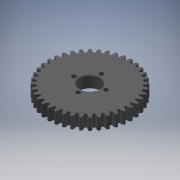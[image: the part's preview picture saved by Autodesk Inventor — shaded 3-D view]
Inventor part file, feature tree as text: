
AUTODESK INVENTOR PART (.ipt)
format: ipt  version: 2016 (Build 200138000, 138)  size: 1,243,136 bytes
history: native  units: mm
features: other x14, sketch x4, revolve x3, extrude x2, hole x1
ambient origin geometry x8: Origin, YZ Plane, XZ Plane, XY Plane, X Axis, Y Axis, Z Axis, Center Point
bodies: Solid1 (feature_tree)
feature tree (24):
  revolve  "Revolution1"  [1 undecoded]
  extrude  "Extrusion1"  TaperAngle=360.0deg  [1 undecoded]
  hole  "Hole1"  [1 undecoded]
  revolve  "Revolution2"  [1 undecoded]
  revolve  "Revolution3"  [1 undecoded]
  other  "b_XY"
  other  "b_YZ"
  other  "b_ZX"
  other  "b_X"
  other  "b_Y"
  other  "b_Z"
  other  "b_Center"
  other  "turn_around_XY"
  other  "turn_around_YZ"
  other  "turn_around_ZX"
  other  "turn_around_X"
  other  "turn_around_Y"
  other  "turn_around_Z"
  other  "turn_around_Center"
  extrude  "押し出し2"  Depth=6.0mm
  sketch  "Sketch_12"  dims[d11=360.0deg d12=0.0mm d13=14.0mm d14=2.2mm d15=2.2mm d16=2.2mm d17=2.2mm d18=6.0mm d19=0.0mm]
  sketch  "Sketch_3"  dims[d0=360.0deg d1=6.0mm d2=0.0mm]
  sketch  "Sketch3"  dims[d3=10.0mm d4=6.0mm d5=4.0mm d6=2.0mm d7=90.0deg d8=6.0mm d9=0.0mm d10=360.0deg]
  sketch  "スケッチ6"
note: 5 required parameter values undecoded (feature->parameter linkage not recoverable at this tier; creation-order binding heuristic only, values carry confidence <= 0.55)